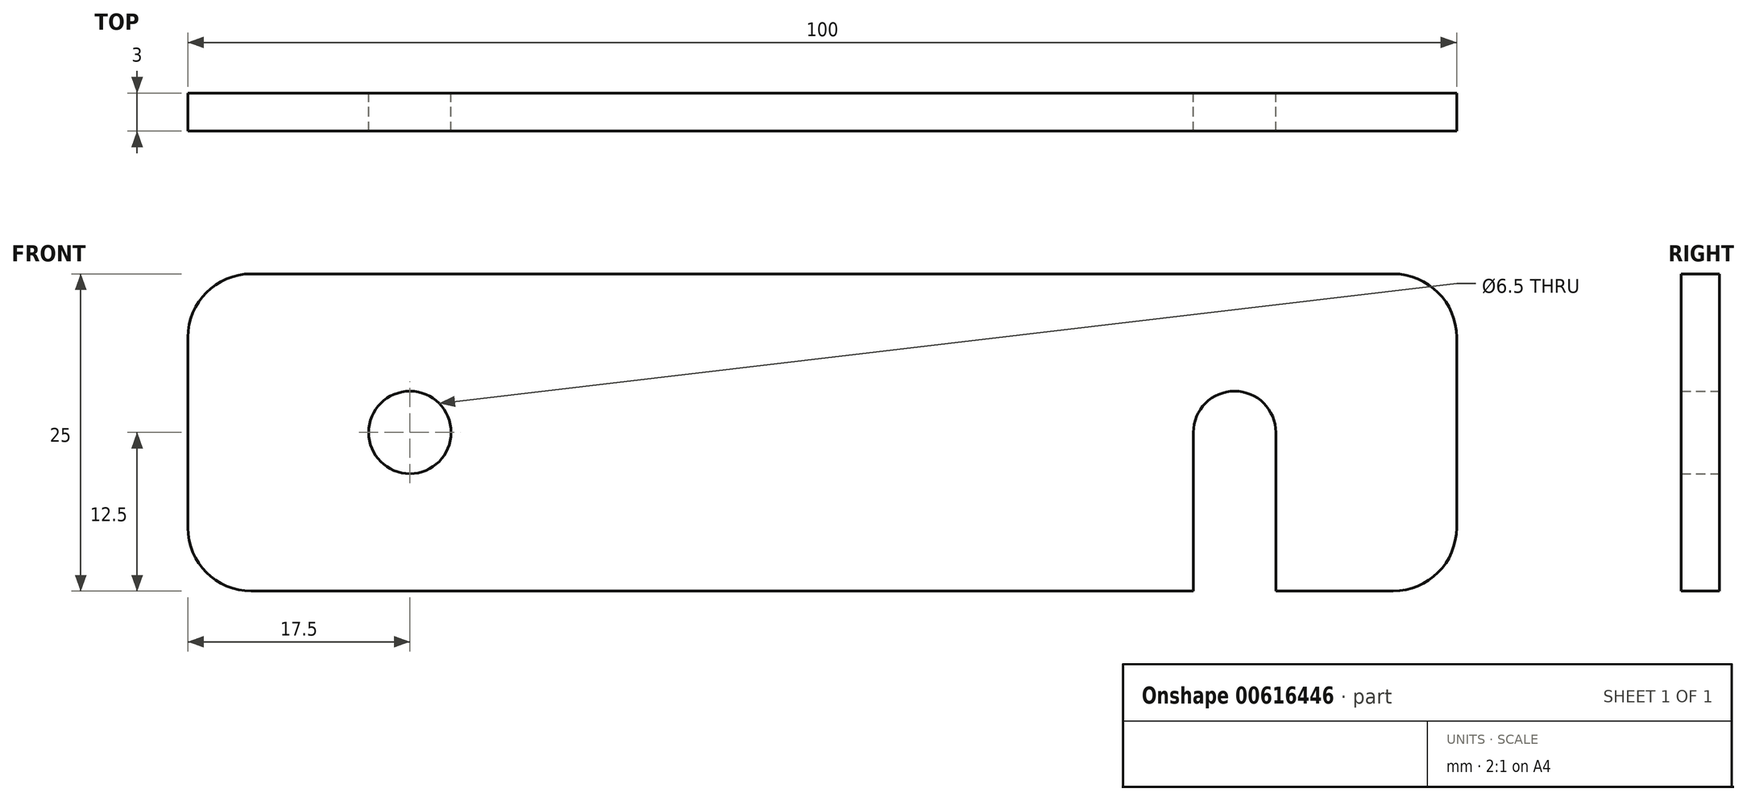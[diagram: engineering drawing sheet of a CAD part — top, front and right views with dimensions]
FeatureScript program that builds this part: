
annotation { "Feature Type Name" : "Feature", "Feature Type Description" : "" }
export const myFeature = defineFeature(function(context is Context, id is Id, definition is map)
    precondition{}
    {
        {
            var Q0;
            Q0=qCreatedBy(makeId("Front.planeOp"),FACE);
            var sketch = newSketch(context, id + "F0", { "sketchPlane" : qUnion([Q0])});
            skLineSegment(sketch, "E0.bottom", {"start": v(-50, -12.5) * mm, "end": v(50, -12.5) * mm});
            skLineSegment(sketch, "E0.top", {"start": v(-50, 12.5) * mm, "end": v(50, 12.5) * mm});
            skLineSegment(sketch, "E0.left", {"start": v(-50, -12.5) * mm, "end": v(-50, 12.5) * mm});
            skLineSegment(sketch, "E0.right", {"start": v(50, -12.5) * mm, "end": v(50, 12.5) * mm});
            skPoint(sketch, "E0.middle", {"position": v(0, 0) * mm});
            skSolve(sketch);
        }
        {
            var Q0;
            Q0 = qSketchRegion(id + "F0", true);
            extrude(context, id + "F1", {"entities" : qUnion([Q0]), "depth" : 3 * mm, "offsetDistance" : 25 * mm});
        }
        {
            var Q0;
            Q0=makeQuery(id+"F1.opExtrude","SWEPT_EDGE",EDGE,{"disambiguationData":[OSD([sQuery(id+"F0.wireOp",EDGE,"E0.top"),sQuery(id+"F0.wireOp",EDGE,"E0.right")])]});
            var Q1;
            Q1=makeQuery(id+"F1.opExtrude","SWEPT_EDGE",EDGE,{"disambiguationData":[OSD([sQuery(id+"F0.wireOp",EDGE,"E0.bottom"),sQuery(id+"F0.wireOp",EDGE,"E0.right")])]});
            var Q2;
            Q2=makeQuery(id+"F1.opExtrude","SWEPT_EDGE",EDGE,{"disambiguationData":[OSD([sQuery(id+"F0.wireOp",EDGE,"E0.bottom"),sQuery(id+"F0.wireOp",EDGE,"E0.left")])]});
            var Q3;
            Q3=makeQuery(id+"F1.opExtrude","SWEPT_EDGE",EDGE,{"disambiguationData":[OSD([sQuery(id+"F0.wireOp",EDGE,"E0.top"),sQuery(id+"F0.wireOp",EDGE,"E0.left")])]});
            fillet(context, id + "F2", {"entities" : qUnion([Q0, Q1, Q2, Q3]), "radius" : 5 * mm, "tangentPropagation" : true, "allowEdgeOverflow" : false});
        }
        {
            var Q0;
            Q0=qCreatedBy(makeId("Front.planeOp"),FACE);
            var sketch = newSketch(context, id + "F3", { "sketchPlane" : qUnion([Q0])});
            skArc(sketch, "E1", {"start": v(35.75, 0) * mm, "mid": v(32.5, 3.25) * mm, "end": v(29.25, 0) * mm});
            skCircle(sketch, "E2.MirrorC", {"center": v(-32.5, 0) * mm, "radius": 3.25 * mm});
            skLineSegment(sketch, "E3", {"start": v(29.25, 0) * mm, "end": v(29.25, -17.69) * mm});
            skLineSegment(sketch, "E4", {"start": v(29.25, -17.69) * mm, "end": v(35.75, -17.69) * mm});
            skLineSegment(sketch, "E5", {"start": v(35.75, 0) * mm, "end": v(35.75, -17.69) * mm});
            skSolve(sketch);
        }
        {
            var Q0;
            Q0 = qSketchRegion(id + "F3", true);
            extrude(context, id + "F4", {"entities" : qUnion([Q0]), "operationType" : NewBodyOperationType.REMOVE, "depth" : 25 * mm, "offsetDistance" : 25 * mm});
        }
    });
